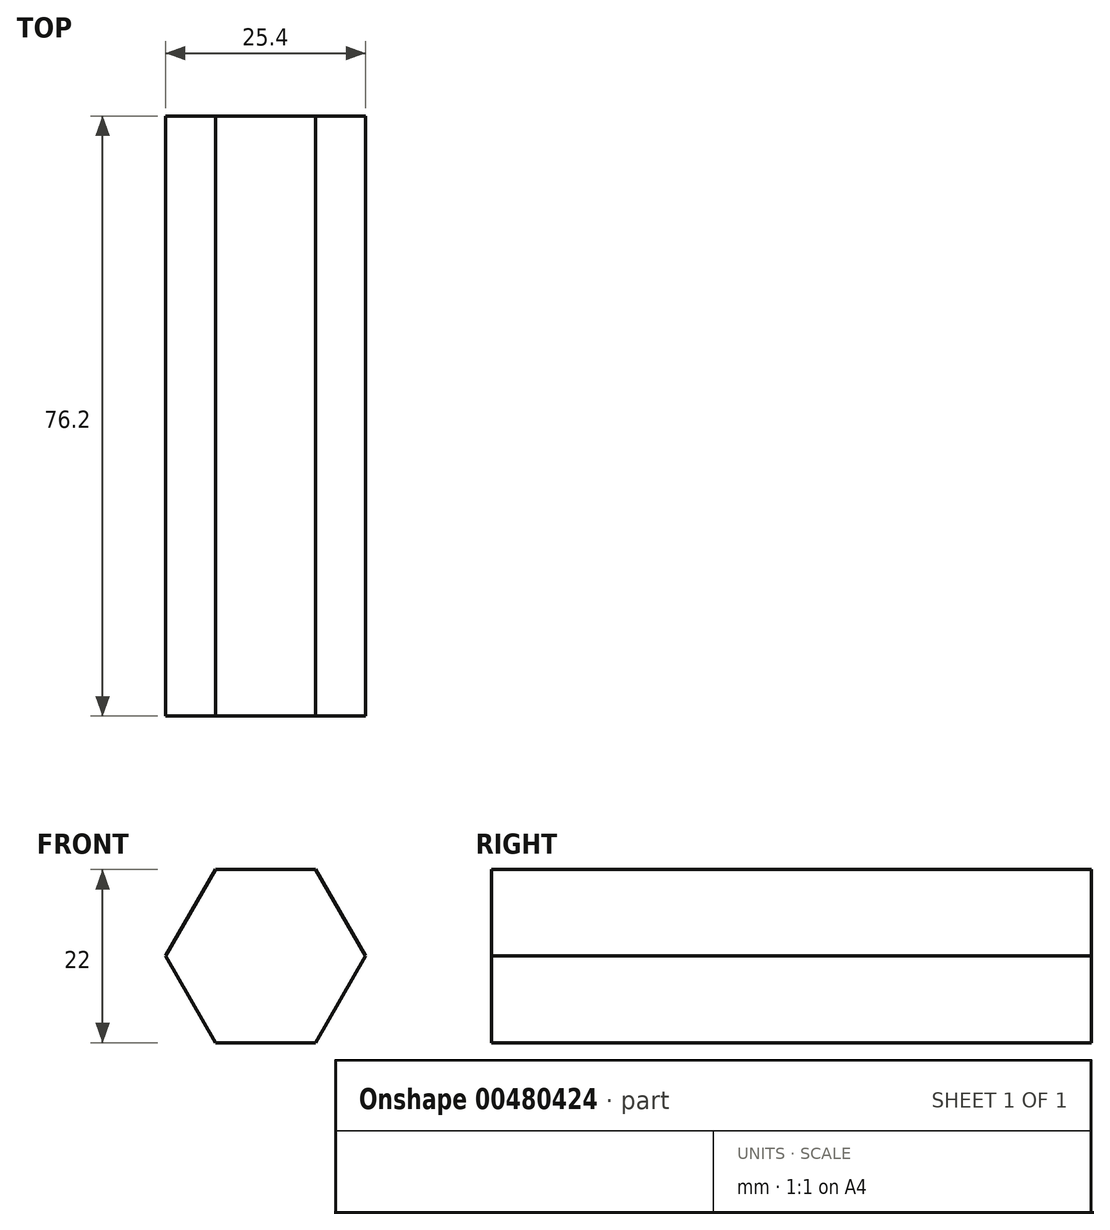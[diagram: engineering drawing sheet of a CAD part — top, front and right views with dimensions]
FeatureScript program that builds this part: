
annotation { "Feature Type Name" : "Feature", "Feature Type Description" : "" }
export const myFeature = defineFeature(function(context is Context, id is Id, definition is map)
    precondition{}
    {
        {
            var Q0;
            Q0=qCreatedBy(makeId("Front.planeOp"),FACE);
            var sketch = newSketch(context, id + "F0", { "sketchPlane" : qUnion([Q0])});
            skCircle(sketch, "E0.cCircle", {"center": v(0, 0) * mm, "radius": 11 * mm, "construction": true});
            skLineSegment(sketch, "E0.0", {"start": v(-6.35, 11) * mm, "end": v(6.35, 11) * mm});
            skLineSegment(sketch, "E0.1", {"start": v(6.35, 11) * mm, "end": v(12.7, 0) * mm});
            skLineSegment(sketch, "E0.2", {"start": v(12.7, 0) * mm, "end": v(6.35, -11) * mm});
            skLineSegment(sketch, "E0.3", {"start": v(6.35, -11) * mm, "end": v(-6.35, -11) * mm});
            skLineSegment(sketch, "E0.4", {"start": v(-6.35, -11) * mm, "end": v(-12.7, 0) * mm});
            skLineSegment(sketch, "E0.5", {"start": v(-12.7, 0) * mm, "end": v(-6.35, 11) * mm});
            skPoint(sketch, "E0.0.midPoint", {"position": v(0, 11) * mm});
            skSolve(sketch);
        }
        {
            var Q0;
            Q0 = qSketchRegion(id + "F0", true);
            extrude(context, id + "F1", {"entities" : qUnion([Q0]), "depth" : 76.2 * mm});
        }
    });
